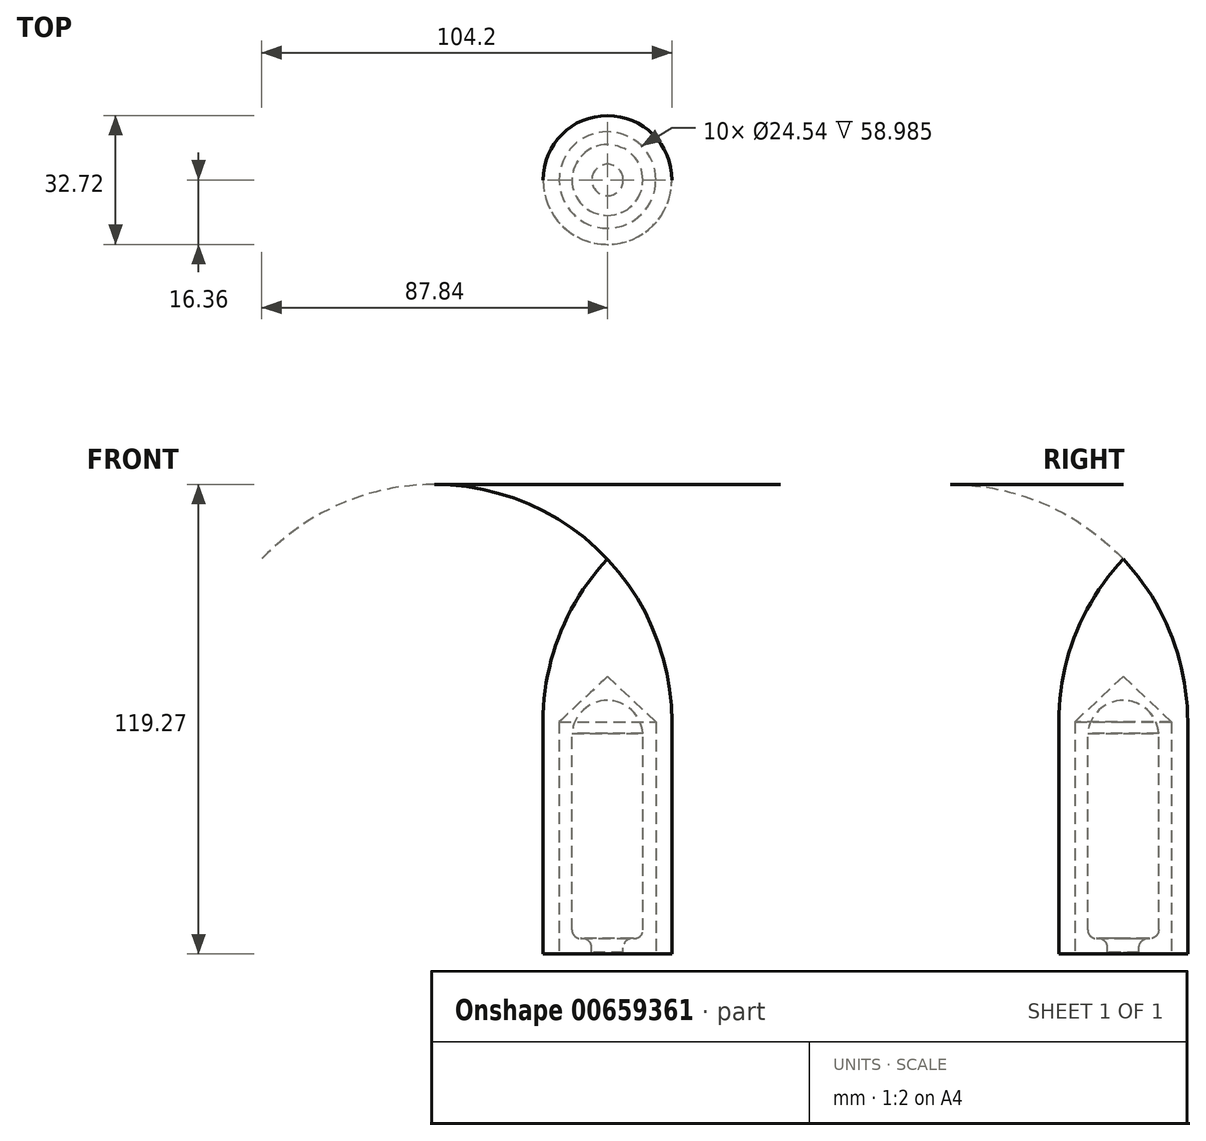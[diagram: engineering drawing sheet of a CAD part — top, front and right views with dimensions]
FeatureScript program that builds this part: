
annotation { "Feature Type Name" : "Feature", "Feature Type Description" : "" }
export const myFeature = defineFeature(function(context is Context, id is Id, definition is map)
    precondition{}
    {
        {
            var Q0;
            Q0=qCreatedBy(makeId("Right.planeOp"),FACE);
            var sketch = newSketch(context, id + "F0", { "sketchPlane" : qUnion([Q0])});
            skLineSegment(sketch, "E0", {"start": v(0, 22.97) * mm, "end": v(0, -41.03) * mm});
            skLineSegment(sketch, "E1", {"start": v(0, -41.03) * mm, "end": v(4, -41.03) * mm});
            skLineSegment(sketch, "E2", {"start": v(4, -41.03) * mm, "end": v(4, -39.87) * mm});
            skArc(sketch, "E3", {"start": v(9, 14.64) * mm, "mid": v(6.13, 20.57) * mm, "end": v(0, 22.97) * mm});
            skLineSegment(sketch, "E4", {"start": v(9, 14.64) * mm, "end": v(9, -35.36) * mm});
            skArc(sketch, "E5", {"start": v(6.61, -37.51) * mm, "mid": v(8.29, -36.97) * mm, "end": v(9, -35.36) * mm});
            skArc(sketch, "E6", {"start": v(6.61, -37.51) * mm, "mid": v(4.78, -38.1) * mm, "end": v(4, -39.87) * mm});
            skSolve(sketch);
        }
        {
            var Q0;
            Q0 = qSketchRegion(id + "F0", true);
            var Q1;
            Q1=sQuery(id+"F0.wireOp",EDGE,"E0");
            revolve(context, id + "F1", {"entities" : qUnion([Q0]), "axis" : qUnion([Q1]), "revolveType" : RevolveType.FULL});
        }
        {
            var Q0;
            Q0=qCreatedBy(makeId("Right.planeOp"),FACE);
            var sketch = newSketch(context, id + "F2", { "sketchPlane" : qUnion([Q0])});
            skLineSegment(sketch, "E7", {"start": v(0, -41.16) * mm, "end": v(0, 58.85) * mm});
            skLineSegment(sketch, "E8", {"start": v(0, 29.02) * mm, "end": v(12.27, 17.55) * mm});
            skLineSegment(sketch, "E9", {"start": v(12.27, 17.55) * mm, "end": v(12.27, -41.43) * mm});
            skLineSegment(sketch, "E10", {"start": v(12.27, -41.43) * mm, "end": v(16.36, -41.43) * mm});
            skLineSegment(sketch, "E11", {"start": v(16.36, -41.43) * mm, "end": v(16.36, 17.55) * mm});
            skArc(sketch, "E12", {"start": v(16.36, 17.55) * mm, "mid": v(12.12, 39.76) * mm, "end": v(0, 58.85) * mm});
            skSolve(sketch);
        }
        {
            var Q0;
            Q0 = qSketchRegion(id + "F2", true);
            var Q1;
            Q1=sQuery(id+"F2.wireOp",EDGE,"E7");
            revolve(context, id + "F3", {"entities" : qUnion([Q0]), "axis" : qUnion([Q1]), "revolveType" : RevolveType.FULL});
        }
    });
